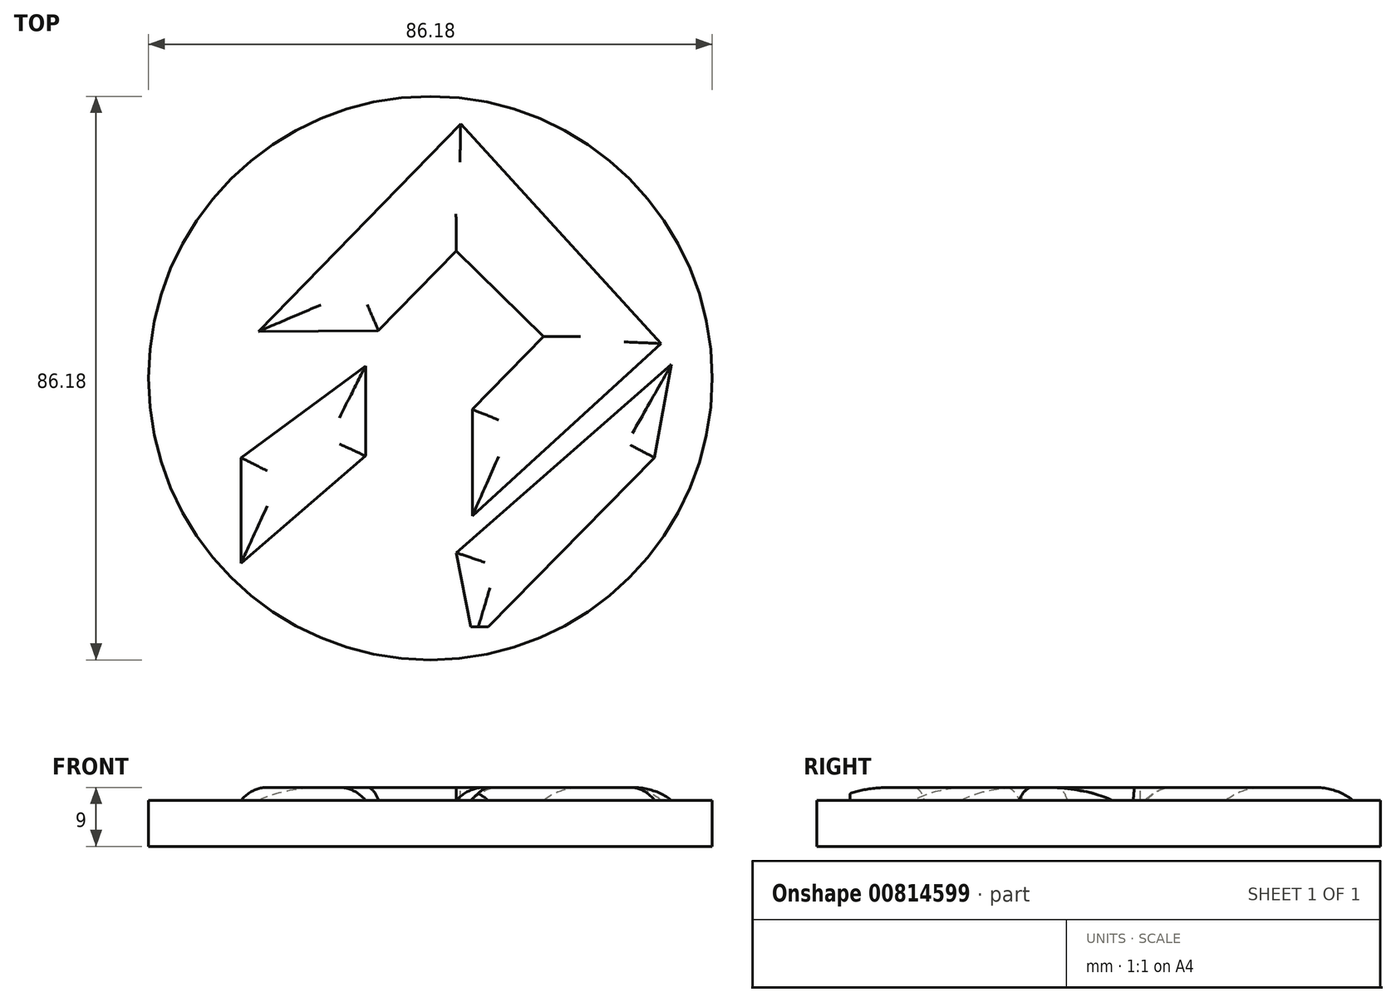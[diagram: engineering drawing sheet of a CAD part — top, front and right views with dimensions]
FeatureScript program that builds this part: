
annotation { "Feature Type Name" : "Feature", "Feature Type Description" : "" }
export const myFeature = defineFeature(function(context is Context, id is Id, definition is map)
    precondition{}
    {
        {
            var Q0;
            Q0=qCreatedBy(makeId("Top.planeOp"),FACE);
            var sketch = newSketch(context, id + "F0", { "sketchPlane" : qUnion([Q0])});
            skLineSegment(sketch, "E0", {"start": v(-28.94, -2.25) * mm, "end": v(-28.94, -18.37) * mm});
            skLineSegment(sketch, "E1", {"start": v(-28.94, -18.37) * mm, "end": v(-9.9, -1.98) * mm});
            skLineSegment(sketch, "E2", {"start": v(-9.9, -1.98) * mm, "end": v(-9.9, 11.76) * mm});
            skLineSegment(sketch, "E3", {"start": v(-9.9, 11.76) * mm, "end": v(-28.94, -2.25) * mm});
            skLineSegment(sketch, "E4", {"start": v(-26.3, 17.04) * mm, "end": v(4.62, 48.76) * mm});
            skLineSegment(sketch, "E5", {"start": v(4.62, 48.76) * mm, "end": v(35.28, 15.2) * mm});
            skLineSegment(sketch, "E6", {"start": v(35.28, 15.2) * mm, "end": v(6.42, -11.17) * mm});
            skLineSegment(sketch, "E7", {"start": v(6.42, -11.17) * mm, "end": v(6.42, 5.15) * mm});
            skLineSegment(sketch, "E8", {"start": v(6.42, 5.15) * mm, "end": v(17.3, 16.25) * mm});
            skLineSegment(sketch, "E9", {"start": v(17.3, 16.25) * mm, "end": v(3.97, 29.34) * mm});
            skLineSegment(sketch, "E10", {"start": v(3.97, 29.34) * mm, "end": v(-7.95, 17.19) * mm});
            skLineSegment(sketch, "E11", {"start": v(-7.95, 17.19) * mm, "end": v(-26.3, 17.04) * mm});
            skLineSegment(sketch, "E12", {"start": v(8.85, -28.14) * mm, "end": v(34.27, -2.25) * mm});
            skLineSegment(sketch, "E13", {"start": v(34.27, -2.25) * mm, "end": v(36.86, 12.02) * mm});
            skLineSegment(sketch, "E14", {"start": v(36.86, 12.02) * mm, "end": v(3.97, -16.78) * mm});
            skLineSegment(sketch, "E15", {"start": v(3.97, -16.78) * mm, "end": v(6.21, -28.14) * mm});
            skLineSegment(sketch, "E16", {"start": v(6.21, -28.14) * mm, "end": v(8.85, -28.14) * mm});
            skSolve(sketch);
        }
        {
            var Q0;
            Q0=qCreatedBy(makeId("Top.planeOp"),FACE);
            var sketch = newSketch(context, id + "F1", { "sketchPlane" : qUnion([Q0])});
            skCircle(sketch, "E17", {"center": v(0, 9.9) * mm, "radius": 43.09 * mm});
            skSolve(sketch);
        }
        {
            var Q0;
            Q0 = qSketchRegion(id + "F1", true);
            extrude(context, id + "F2", {"entities" : qUnion([Q0]), "depth" : 7 * mm, "offsetDistance" : 25 * mm});
        }
        {
            var Q0;
            Q0=makeQuery(id+"F0.imprint","IMPRINT",FACE,{"disambiguationData":[TD([[makeQuery(id+"F0.imprint","IMPRINT",EDGE,{"derivedFrom":sQuery(id+"F0.wireOp",EDGE,"E4")}),-1.0]])]});
            var Q1;
            Q1=makeQuery(id+"F0.imprint","IMPRINT",FACE,{"disambiguationData":[TD([[makeQuery(id+"F0.imprint","IMPRINT",EDGE,{"derivedFrom":sQuery(id+"F0.wireOp",EDGE,"E0")}),1.0]])]});
            var Q2;
            Q2=makeQuery(id+"F0.imprint","IMPRINT",FACE,{"disambiguationData":[TD([[makeQuery(id+"F0.imprint","IMPRINT",EDGE,{"derivedFrom":sQuery(id+"F0.wireOp",EDGE,"E12")}),1.0]])]});
            extrude(context, id + "F3", {"entities" : qUnion([Q0, Q1, Q2]), "operationType" : NewBodyOperationType.ADD, "depth" : 9 * mm, "offsetDistance" : 25 * mm});
        }
        {
            var Q0;
            Q0=makeQuery(id+"F3.opExtrude","CAP_FACE",FACE,{"disambiguationData":[OSD([sQuery(id+"F0.wireOp",EDGE,"E4"),sQuery(id+"F0.wireOp",EDGE,"E5"),sQuery(id+"F0.wireOp",EDGE,"E6"),sQuery(id+"F0.wireOp",EDGE,"E7"),sQuery(id+"F0.wireOp",EDGE,"E8"),sQuery(id+"F0.wireOp",EDGE,"E9"),sQuery(id+"F0.wireOp",EDGE,"E10"),sQuery(id+"F0.wireOp",EDGE,"E11")])],"isStart":false});
            var Q1;
            Q1=makeQuery(id+"F3.opExtrude","CAP_FACE",FACE,{"disambiguationData":[OSD([sQuery(id+"F0.wireOp",EDGE,"E0"),sQuery(id+"F0.wireOp",EDGE,"E1"),sQuery(id+"F0.wireOp",EDGE,"E2"),sQuery(id+"F0.wireOp",EDGE,"E3")])],"isStart":false});
            var Q2;
            Q2=makeQuery(id+"F3.opExtrude","CAP_FACE",FACE,{"disambiguationData":[OSD([sQuery(id+"F0.wireOp",EDGE,"E12"),sQuery(id+"F0.wireOp",EDGE,"E13"),sQuery(id+"F0.wireOp",EDGE,"E14"),sQuery(id+"F0.wireOp",EDGE,"E15"),sQuery(id+"F0.wireOp",EDGE,"E16")])],"isStart":false});
            fillet(context, id + "F4", {"entities" : qUnion([Q0, Q1, Q2]), "radius" : 5 * mm, "tangentPropagation" : true, "allowEdgeOverflow" : false});
        }
    });
